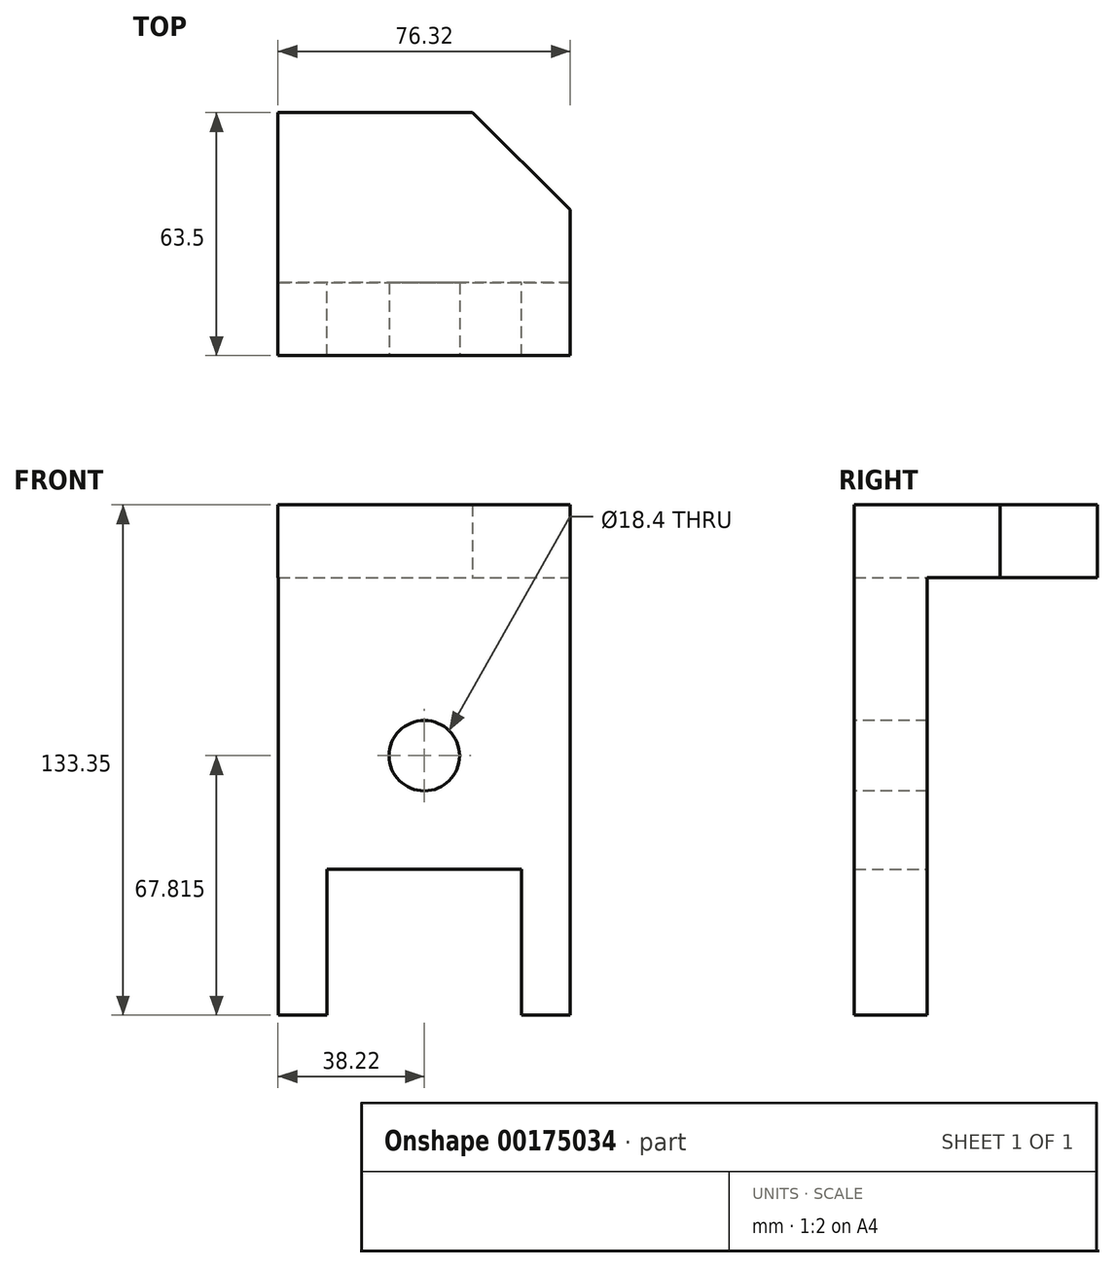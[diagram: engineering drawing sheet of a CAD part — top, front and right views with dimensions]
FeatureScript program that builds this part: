
annotation { "Feature Type Name" : "Feature", "Feature Type Description" : "" }
export const myFeature = defineFeature(function(context is Context, id is Id, definition is map)
    precondition{}
    {
        {
            var Q0;
            Q0=qCreatedBy(makeId("Front.planeOp"),FACE);
            var sketch = newSketch(context, id + "F0", { "sketchPlane" : qUnion([Q0])});
            skLineSegment(sketch, "E0", {"start": v(-38.1, 48.76) * mm, "end": v(38.1, 48.76) * mm});
            skLineSegment(sketch, "E1", {"start": v(38.1, 48.76) * mm, "end": v(38.1, -65.54) * mm});
            skLineSegment(sketch, "E2", {"start": v(38.1, -65.54) * mm, "end": v(25.4, -65.54) * mm});
            skLineSegment(sketch, "E3", {"start": v(25.4, -65.54) * mm, "end": v(25.4, -27.44) * mm});
            skLineSegment(sketch, "E4", {"start": v(25.4, -27.44) * mm, "end": v(-25.4, -27.44) * mm});
            skLineSegment(sketch, "E5", {"start": v(-25.4, -27.44) * mm, "end": v(-25.4, -65.54) * mm});
            skLineSegment(sketch, "E6", {"start": v(-25.4, -65.54) * mm, "end": v(-38.1, -65.54) * mm});
            skLineSegment(sketch, "E7", {"start": v(-38.1, -65.54) * mm, "end": v(-38.1, 48.76) * mm});
            skPoint(sketch, "E8", {"position": v(0, 48.76) * mm});
            skSolve(sketch);
        }
        {
            var Q0;
            Q0 = qSketchRegion(id + "F0", true);
            extrude(context, id + "F1", {"entities" : qUnion([Q0]), "depth" : 19.05 * mm});
        }
        {
            var Q0;
            Q0=makeQuery(id+"F1.opExtrude","CAP_FACE",FACE,{"disambiguationData":[OSD([sQuery(id+"F0.wireOp",EDGE,"E0"),sQuery(id+"F0.wireOp",EDGE,"E1"),sQuery(id+"F0.wireOp",EDGE,"E2"),sQuery(id+"F0.wireOp",EDGE,"E3"),sQuery(id+"F0.wireOp",EDGE,"E4"),sQuery(id+"F0.wireOp",EDGE,"E5"),sQuery(id+"F0.wireOp",EDGE,"E6"),sQuery(id+"F0.wireOp",EDGE,"E7")])],"isStart":false});
            var sketch = newSketch(context, id + "F2", { "sketchPlane" : qUnion([Q0])});
            skCircle(sketch, "E9", {"center": v(0, 2.28) * mm, "radius": 9.2 * mm});
            skSolve(sketch);
        }
        {
            var Q0;
            Q0 = qSketchRegion(id + "F2", true);
            extrude(context, id + "F3", {"entities" : qUnion([Q0]), "operationType" : NewBodyOperationType.REMOVE, "oppositeDirection" : true, "depth" : 19.05 * mm});
        }
        {
            var Q0;
            Q0=makeQuery(id+"F1.opExtrude","SWEPT_FACE",FACE,{"disambiguationData":[OSD([sQuery(id+"F0.wireOp",EDGE,"E0")])]});
            var sketch = newSketch(context, id + "F4", { "sketchPlane" : qUnion([Q0])});
            skPoint(sketch, "E10", {"position": v(0, -19.05) * mm});
            skLineSegment(sketch, "E11", {"start": v(-38.22, -19.05) * mm, "end": v(-38.22, 44.45) * mm});
            skLineSegment(sketch, "E12", {"start": v(-38.22, 44.45) * mm, "end": v(12.58, 44.45) * mm});
            skLineSegment(sketch, "E13", {"start": v(12.58, 44.45) * mm, "end": v(38.1, 19.05) * mm});
            skLineSegment(sketch, "E14", {"start": v(38.1, 19.05) * mm, "end": v(38.1, -19.05) * mm});
            skLineSegment(sketch, "E15", {"start": v(38.1, -19.05) * mm, "end": v(-38.22, -19.05) * mm});
            skSolve(sketch);
        }
        {
            var Q0;
            Q0 = qSketchRegion(id + "F4", true);
            extrude(context, id + "F5", {"entities" : qUnion([Q0]), "operationType" : NewBodyOperationType.ADD, "depth" : 19.05 * mm});
        }
    });
